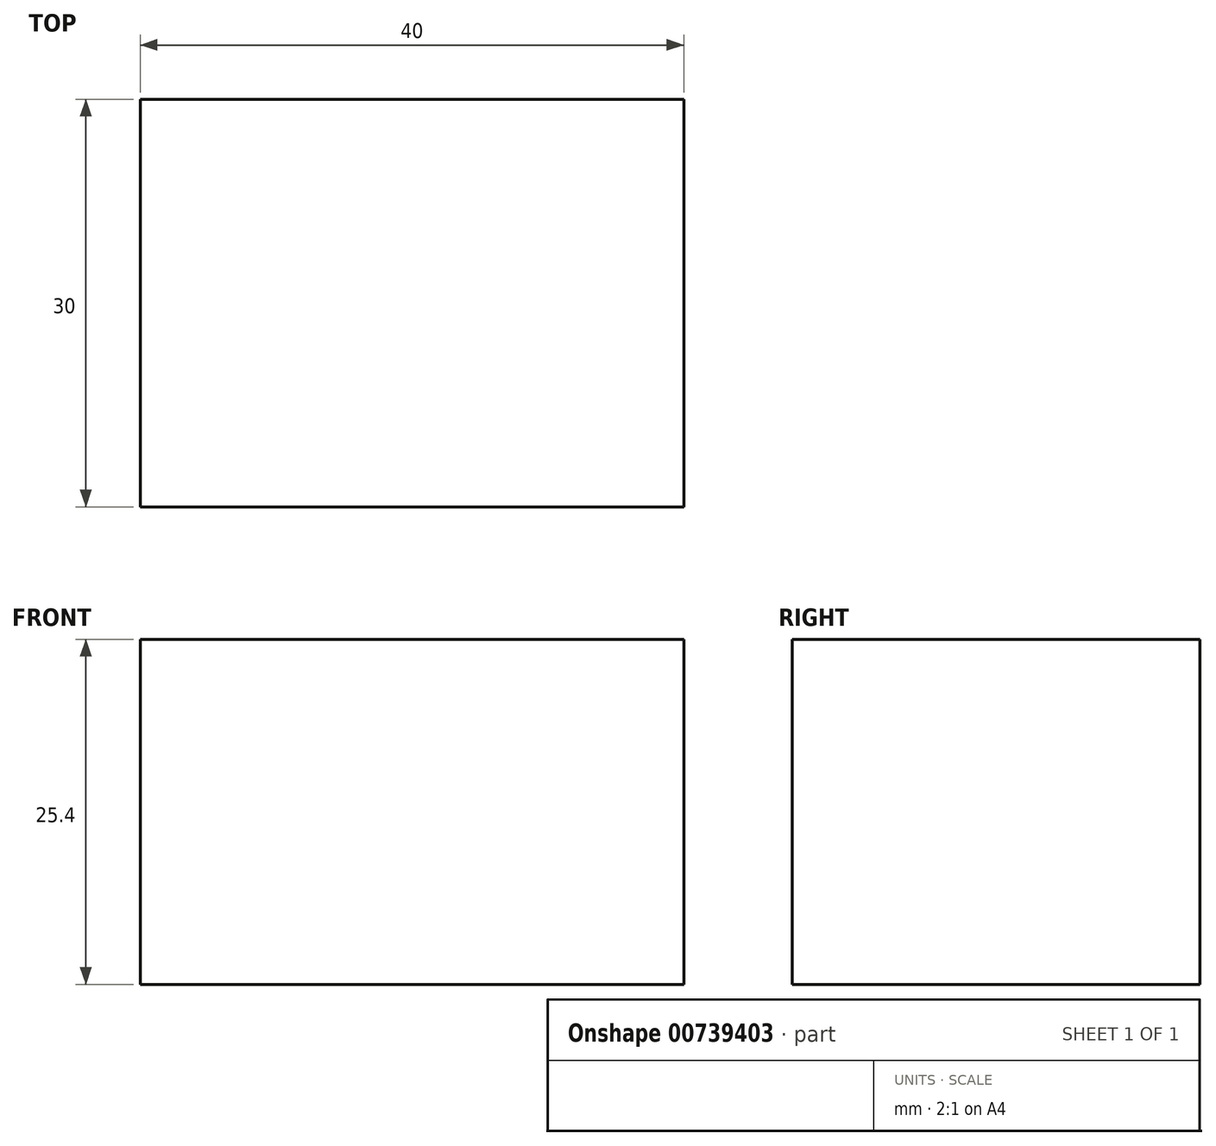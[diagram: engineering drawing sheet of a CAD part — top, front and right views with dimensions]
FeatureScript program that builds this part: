
annotation { "Feature Type Name" : "Feature", "Feature Type Description" : "" }
export const myFeature = defineFeature(function(context is Context, id is Id, definition is map)
    precondition{}
    {
        {
            var Q0;
            Q0=qCreatedBy(makeId("Top.planeOp"),FACE);
            var sketch = newSketch(context, id + "F0", { "sketchPlane" : qUnion([Q0])});
            skLineSegment(sketch, "E0.bottom", {"start": v(20, 15) * mm, "end": v(-20, 15) * mm});
            skLineSegment(sketch, "E0.top", {"start": v(20, -15) * mm, "end": v(-20, -15) * mm});
            skLineSegment(sketch, "E0.left", {"start": v(20, 15) * mm, "end": v(20, -15) * mm});
            skLineSegment(sketch, "E0.right", {"start": v(-20, 15) * mm, "end": v(-20, -15) * mm});
            skPoint(sketch, "E0.middle", {"position": v(0, 0) * mm});
            skSolve(sketch);
        }
        {
            var Q0;
            Q0 = qSketchRegion(id + "F0", true);
            extrude(context, id + "F1", {"entities" : qUnion([Q0]), "depth" : 25.4 * mm, "offsetDistance" : 25.4 * mm});
        }
    });
